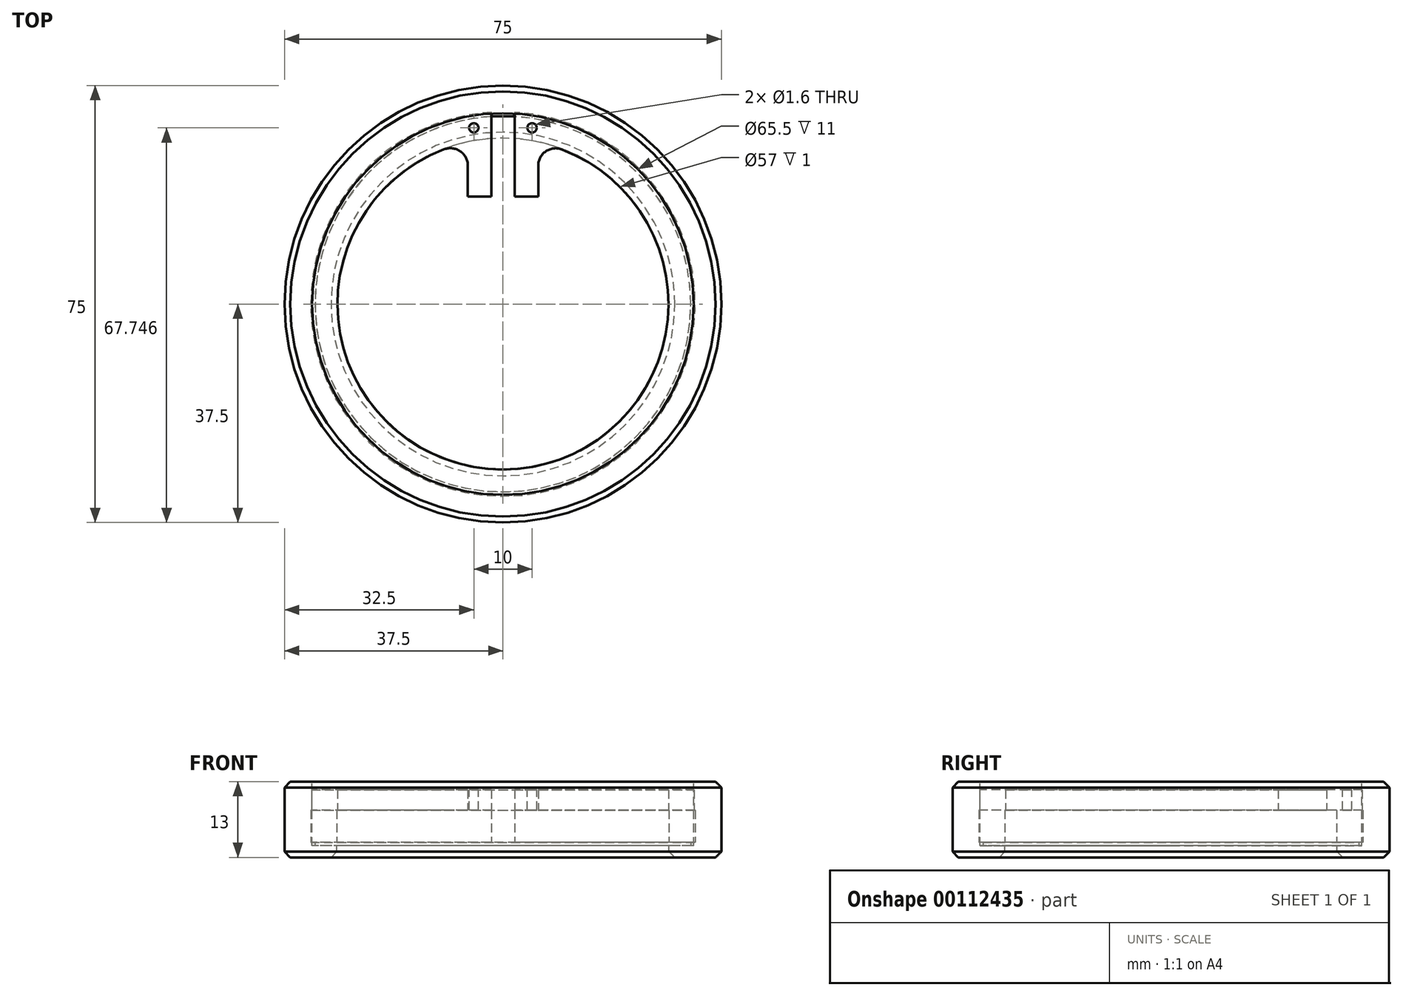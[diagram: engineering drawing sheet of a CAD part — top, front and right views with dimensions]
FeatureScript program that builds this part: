
annotation { "Feature Type Name" : "Feature", "Feature Type Description" : "" }
export const myFeature = defineFeature(function(context is Context, id is Id, definition is map)
    precondition{}
    {
        {
            var Q0;
            Q0=qCreatedBy(makeId("Top.planeOp"),FACE);
            var sketch = newSketch(context, id + "F0", { "sketchPlane" : qUnion([Q0])});
            skCircle(sketch, "E0", {"center": v(0, 0) * mm, "radius": 37.5 * mm});
            skSolve(sketch);
        }
        {
            var Q0;
            Q0=makeQuery(id+"F0.imprint","IMPRINT",FACE,{"disambiguationData":[TD([[makeQuery(id+"F0.imprint","IMPRINT",EDGE,{"derivedFrom":sQuery(id+"F0.wireOp",EDGE,"E0")}),1.0]])]});
            extrude(context, id + "F1", {"entities" : qUnion([Q0]), "depth" : 13 * mm});
        }
        {
            var Q0;
            Q0=makeQuery(id+"F1.opExtrude","CAP_FACE",FACE,{"disambiguationData":[OSD([sQuery(id+"F0.wireOp",EDGE,"E0")])],"isStart":false});
            var sketch = newSketch(context, id + "F2", { "sketchPlane" : qUnion([Q0])});
            skCircle(sketch, "E1", {"center": v(0, 0) * mm, "radius": 32.75 * mm});
            skSolve(sketch);
        }
        {
            var Q0;
            Q0=qSketchRegion(id+"F2",true);
            extrude(context, id + "F3", {"entities" : qUnion([Q0]), "operationType" : NewBodyOperationType.REMOVE, "oppositeDirection" : true, "depth" : 11 * mm});
        }
        {
            var Q0;
            Q0=makeQuery(id+"F3.boolean.opBoolean","COPY",FACE,{"derivedFrom":makeQuery(id+"F3.opExtrude","CAP_FACE",FACE,{"disambiguationData":[OSD([sQuery(id+"F2.wireOp",EDGE,"E1")])],"isStart":false})});
            var sketch = newSketch(context, id + "F4", { "sketchPlane" : qUnion([Q0])});
            skCircle(sketch, "E2", {"center": v(0, 0) * mm, "radius": 28.5 * mm});
            skSolve(sketch);
        }
        {
            var Q0;
            Q0=qSketchRegion(id+"F4",true);
            extrude(context, id + "F5", {"entities" : qUnion([Q0]), "operationType" : NewBodyOperationType.REMOVE, "oppositeDirection" : true, "depth" : 25 * mm});
        }
        {
            var Q0;
            Q0=makeQuery(id+"F3.boolean.opBoolean","COPY",FACE,{"derivedFrom":makeQuery(id+"F3.opExtrude","CAP_FACE",FACE,{"disambiguationData":[OSD([sQuery(id+"F2.wireOp",EDGE,"E1")])],"isStart":false})});
            var sketch = newSketch(context, id + "F6", { "sketchPlane" : qUnion([Q0])});
            skCircle(sketch, "E3", {"center": v(0, 0) * mm, "radius": 32.25 * mm});
            skSolve(sketch);
        }
        {
            var Q0;
            Q0=qSketchRegion(id+"F6",true);
            extrude(context, id + "F7", {"entities" : qUnion([Q0]), "depth" : .6 * mm});
        }
        {
            var Q0;
            Q0=makeQuery(id+"F7.opExtrude","CAP_FACE",FACE,{"disambiguationData":[OSD([sQuery(id+"F6.wireOp",EDGE,"E3")])],"isStart":false});
            var sketch = newSketch(context, id + "F8", { "sketchPlane" : qUnion([Q0])});
            skArc(sketch, "E4", {"start": v(-2, 32.94) * mm, "mid": v(0, -33) * mm, "end": v(2, 32.94) * mm});
            skArc(sketch, "E5", {"start": v(-2, 28.43) * mm, "mid": v(0, -28.5) * mm, "end": v(2, 28.43) * mm});
            skLineSegment(sketch, "E6.left", {"start": v(-2, 32.94) * mm, "end": v(-2, 28.43) * mm});
            skLineSegment(sketch, "E6.right", {"start": v(2, 32.94) * mm, "end": v(2, 28.43) * mm});
            skSolve(sketch);
        }
        {
            var Q0;
            Q0=qSketchRegion(id+"F8",true);
            extrude(context, id + "F9", {"entities" : qUnion([Q0]), "depth" : 5.5 * mm});
        }
        {
            var Q0;
            Q0=makeQuery(id+"F9.opExtrude","CAP_FACE",FACE,{"disambiguationData":[OSD([sQuery(id+"F8.wireOp",EDGE,"E4"),sQuery(id+"F8.wireOp",EDGE,"E5"),sQuery(id+"F8.wireOp",EDGE,"E6.left"),sQuery(id+"F8.wireOp",EDGE,"E6.right")])],"isStart":false});
            var sketch = newSketch(context, id + "F10", { "sketchPlane" : qUnion([Q0])});
            skArc(sketch, "E7", {"start": v(-2, 32.78) * mm, "mid": v(0, -32.84) * mm, "end": v(2, 32.78) * mm});
            skArc(sketch, "E8", {"start": v(-10.1, 26.55) * mm, "mid": v(-0.02, -28.4) * mm, "end": v(10.12, 26.54) * mm});
            skLineSegment(sketch, "E9", {"start": v(2, 28.43) * mm, "end": v(2, 18.43) * mm});
            skLineSegment(sketch, "E10", {"start": v(2, 18.43) * mm, "end": v(6.05, 18.43) * mm});
            skLineSegment(sketch, "E11", {"start": v(6.05, 18.43) * mm, "end": v(6.05, 23.73) * mm});
            skLineSegment(sketch, "E12", {"start": v(-2, 28.43) * mm, "end": v(-2, 18.43) * mm});
            skPoint(sketch, "E12.endSnap0", {"position": v(4.03, 18.43) * mm});
            skLineSegment(sketch, "E13", {"start": v(-2, 18.43) * mm, "end": v(-6.03, 18.43) * mm});
            skLineSegment(sketch, "E14", {"start": v(-6.03, 18.43) * mm, "end": v(-6.03, 23.75) * mm});
            skLineSegment(sketch, "E15", {"start": v(-2, 28.43) * mm, "end": v(-2, 32.78) * mm});
            skLineSegment(sketch, "E16", {"start": v(2, 28.33) * mm, "end": v(2, 32.78) * mm});
            skPoint(sketch, "E17.newPointB", {"position": v(-6.03, 27.86) * mm});
            skArc(sketch, "E17.filletArc", {"start": v(-6.03, 23.75) * mm, "mid": v(-7.32, 26.22) * mm, "end": v(-10.1, 26.55) * mm});
            skPoint(sketch, "E18.visualSharp", {"position": v(6.05, 27.75) * mm});
            skArc(sketch, "E18.filletArc", {"start": v(10.12, 26.54) * mm, "mid": v(7.35, 26.2) * mm, "end": v(6.05, 23.73) * mm});
            skSolve(sketch);
        }
        {
            var Q0;
            Q0 = qSketchRegion(id + "F10", true);
            extrude(context, id + "F11", {"entities" : qUnion([Q0]), "depth" : 3.5 * mm});
        }
        {
            var Q0;
            Q0=makeQuery(id+"F1.opExtrude","CAP_EDGE",EDGE,{"disambiguationData":[OSD([sQuery(id+"F0.wireOp",EDGE,"E0")])],"isStart":true});
            var Q1;
            Q1=makeQuery(id+"F1.opExtrude","CAP_EDGE",EDGE,{"disambiguationData":[OSD([sQuery(id+"F0.wireOp",EDGE,"E0")])],"isStart":false});
            var Q2;
            Q2=makeQuery(id+"F3.boolean.opBoolean","COPY",EDGE,{"derivedFrom":makeQuery(id+"F3.opExtrude","CAP_EDGE",EDGE,{"disambiguationData":[OSD([sQuery(id+"F2.wireOp",EDGE,"E1")])],"isStart":true})});
            var Q3;
            Q3=makeQuery(id+"F5.boolean.opBoolean","INTERSECT",EDGE,{"derivedFrom":[makeQuery(id+"F1.opExtrude","CAP_FACE",FACE,{"disambiguationData":[OSD([sQuery(id+"F0.wireOp",EDGE,"E0")])],"isStart":true}),makeQuery(id+"F5.opExtrude","SWEPT_FACE",FACE,{"disambiguationData":[OSD([sQuery(id+"F4.wireOp",EDGE,"E2")])]})]});
            chamfer(context, id + "F12", {"entities" : qUnion([Q0, Q1, Q2, Q3]), "width" : 1 * mm, "tangentPropagation" : true});
        }
        {
            var Q0;
            Q0=makeQuery(id+"F11.opExtrude","CAP_FACE",FACE,{"disambiguationData":[OSD([sQuery(id+"F10.wireOp",EDGE,"E7"),sQuery(id+"F10.wireOp",EDGE,"E8"),sQuery(id+"F10.wireOp",EDGE,"E9"),sQuery(id+"F10.wireOp",EDGE,"E10"),sQuery(id+"F10.wireOp",EDGE,"E11"),sQuery(id+"F10.wireOp",EDGE,"E12"),sQuery(id+"F10.wireOp",EDGE,"E13"),sQuery(id+"F10.wireOp",EDGE,"E14"),sQuery(id+"F10.wireOp",EDGE,"E15"),sQuery(id+"F10.wireOp",EDGE,"E16"),sQuery(id+"F10.wireOp",EDGE,"E17.filletArc"),sQuery(id+"F10.wireOp",EDGE,"E18.filletArc")])],"isStart":false});
            var sketch = newSketch(context, id + "F13", { "sketchPlane" : qUnion([Q0])});
            skCircle(sketch, "E19", {"center": v(5, 30.25) * mm, "radius": 0.8 * mm});
            skCircle(sketch, "E20", {"center": v(-5, 30.25) * mm, "radius": 0.8 * mm});
            skSolve(sketch);
        }
        {
            var Q0;
            Q0 = qSketchRegion(id + "F13", true);
            var Q1;
            Q1=makeQuery(id+"F11.opExtrude","CAP_FACE",FACE,{"disambiguationData":[OSD([sQuery(id+"F10.wireOp",EDGE,"E7"),sQuery(id+"F10.wireOp",EDGE,"E8"),sQuery(id+"F10.wireOp",EDGE,"E9"),sQuery(id+"F10.wireOp",EDGE,"E10"),sQuery(id+"F10.wireOp",EDGE,"E11"),sQuery(id+"F10.wireOp",EDGE,"E12"),sQuery(id+"F10.wireOp",EDGE,"E13"),sQuery(id+"F10.wireOp",EDGE,"E14"),sQuery(id+"F10.wireOp",EDGE,"E15"),sQuery(id+"F10.wireOp",EDGE,"E16"),sQuery(id+"F10.wireOp",EDGE,"E17.filletArc"),sQuery(id+"F10.wireOp",EDGE,"E18.filletArc")])],"isStart":true});
            extrude(context, id + "F14", {"entities" : qUnion([Q0]), "operationType" : NewBodyOperationType.REMOVE, "endBound" : BoundingType.UP_TO_SURFACE, "oppositeDirection" : true, "endBoundEntityFace" : qUnion([Q1]), "depth" : 25 * mm});
        }
    });
